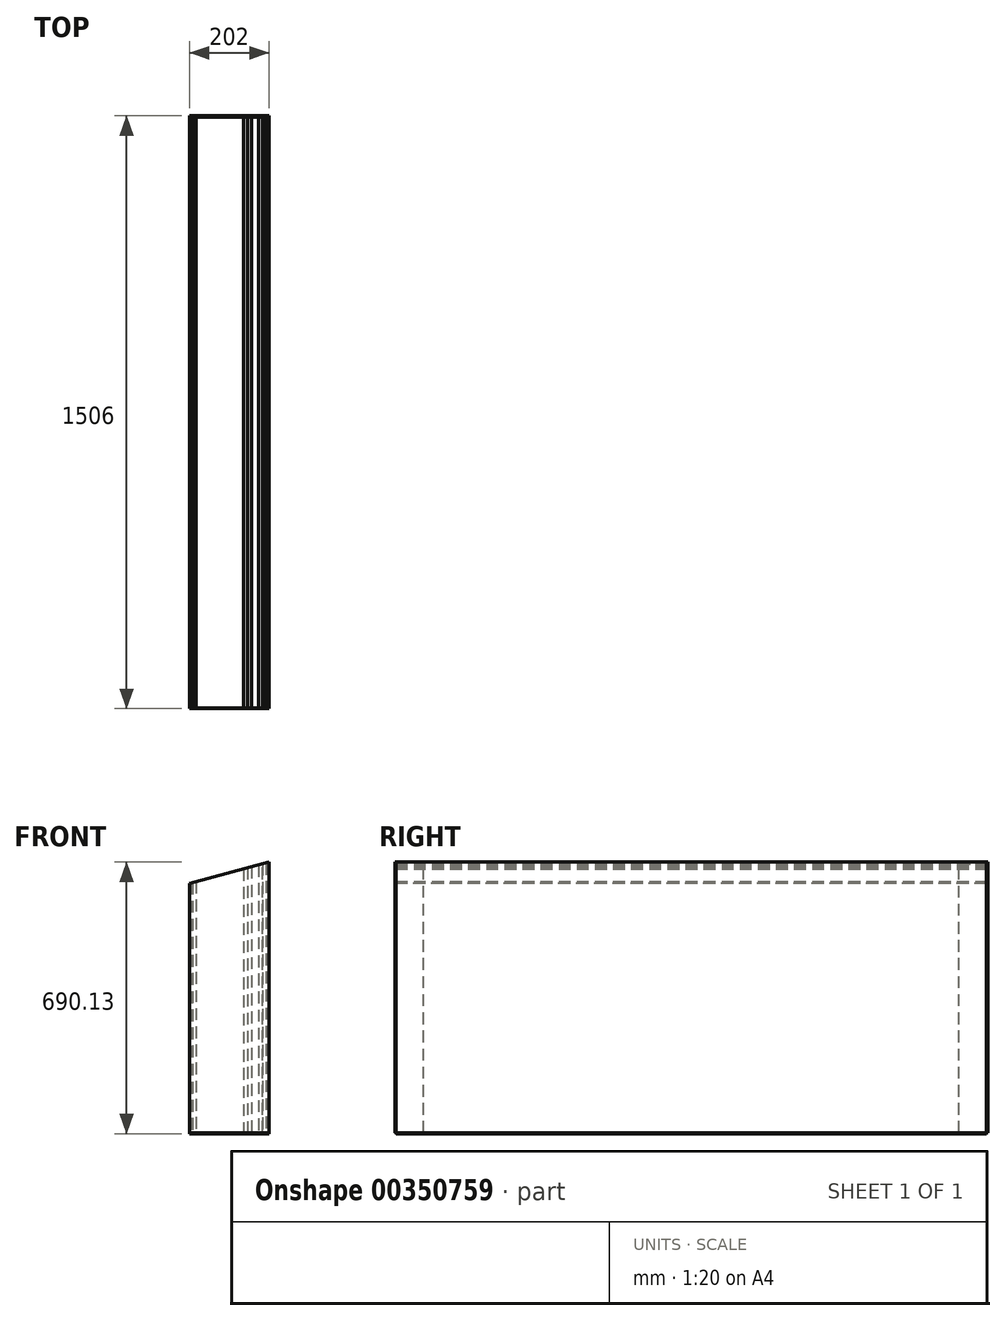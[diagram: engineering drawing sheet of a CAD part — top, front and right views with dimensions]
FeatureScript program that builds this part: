
annotation { "Feature Type Name" : "Feature", "Feature Type Description" : "" }
export const myFeature = defineFeature(function(context is Context, id is Id, definition is map)
    precondition{}
    {
        {
            var Q0;
            Q0=qCreatedBy(makeId("Right.planeOp"),FACE);
            var sketch = newSketch(context, id + "F0", { "sketchPlane" : qUnion([Q0])});
            skLineSegment(sketch, "E0", {"start": v(0, 0) * mm, "end": v(1500, 0) * mm});
            skLineSegment(sketch, "E1", {"start": v(1500, 0) * mm, "end": v(1500, 700) * mm});
            skLineSegment(sketch, "E2", {"start": v(1500, 700) * mm, "end": v(0, 700) * mm});
            skLineSegment(sketch, "E3", {"start": v(0, 700) * mm, "end": v(0, 0) * mm});
            skSolve(sketch);
        }
        {
            var Q0;
            Q0=makeQuery(id+"F0.imprint","IMPRINT",FACE,{"disambiguationData":[TD([[makeQuery(id+"F0.imprint","IMPRINT",EDGE,{"derivedFrom":sQuery(id+"F0.wireOp",EDGE,"E0")}),1.0]])]});
            extrude(context, id + "F1", {"entities" : qUnion([Q0]), "depth" : 6 * mm});
        }
        {
            var Q0;
            Q0=makeQuery(id+"F1.opExtrude","CAP_FACE",FACE,{"disambiguationData":[OSD([sQuery(id+"F0.wireOp",EDGE,"E0"),sQuery(id+"F0.wireOp",EDGE,"E1"),sQuery(id+"F0.wireOp",EDGE,"E2"),sQuery(id+"F0.wireOp",EDGE,"UxQu33BP-PdVc-IvKo-0Oal-Oq9sfbCTzBfW"),sQuery(id+"F0.wireOp",EDGE,"E3")])],"isStart":false});
            extrude(context, id + "F2", {"entities" : qUnion([Q0]), "depth" : 1 * mm});
        }
        {
            var Q0;
            Q0=makeQuery(id+"F2.opExtrude","CAP_FACE",FACE,{"disambiguationData":[OSD([sQuery(id+"F0.wireOp",EDGE,"E0"),sQuery(id+"F0.wireOp",EDGE,"E1"),sQuery(id+"F0.wireOp",EDGE,"E2"),sQuery(id+"F0.wireOp",EDGE,"UxQu33BP-PdVc-IvKo-0Oal-Oq9sfbCTzBfW"),sQuery(id+"F0.wireOp",EDGE,"E3")])],"isStart":false});
            extrude(context, id + "F3", {"entities" : qUnion([Q0]), "depth" : 10 * mm});
        }
        {
            var Q0;
            Q0=makeQuery(id+"F3.opExtrude","CAP_FACE",FACE,{"disambiguationData":[OSD([sQuery(id+"F0.wireOp",EDGE,"E0"),sQuery(id+"F0.wireOp",EDGE,"E1"),sQuery(id+"F0.wireOp",EDGE,"E2"),sQuery(id+"F0.wireOp",EDGE,"UxQu33BP-PdVc-IvKo-0Oal-Oq9sfbCTzBfW"),sQuery(id+"F0.wireOp",EDGE,"E3")])],"isStart":false});
            extrude(context, id + "F4", {"entities" : qUnion([Q0]), "depth" : 120 * mm});
        }
        {
            var Q0;
            Q0=makeQuery(id+"F4.opExtrude","CAP_FACE",FACE,{"disambiguationData":[OSD([sQuery(id+"F0.wireOp",EDGE,"E0"),sQuery(id+"F0.wireOp",EDGE,"E1"),sQuery(id+"F0.wireOp",EDGE,"E2"),sQuery(id+"F0.wireOp",EDGE,"UxQu33BP-PdVc-IvKo-0Oal-Oq9sfbCTzBfW"),sQuery(id+"F0.wireOp",EDGE,"E3")])],"isStart":false});
            extrude(context, id + "F5", {"entities" : qUnion([Q0]), "depth" : 10 * mm});
        }
        {
            var Q0;
            Q0=makeQuery(id+"F5.opExtrude","CAP_FACE",FACE,{"disambiguationData":[OSD([sQuery(id+"F0.wireOp",EDGE,"E0"),sQuery(id+"F0.wireOp",EDGE,"E1"),sQuery(id+"F0.wireOp",EDGE,"E2"),sQuery(id+"F0.wireOp",EDGE,"UxQu33BP-PdVc-IvKo-0Oal-Oq9sfbCTzBfW"),sQuery(id+"F0.wireOp",EDGE,"E3")])],"isStart":false});
            extrude(context, id + "F6", {"entities" : qUnion([Q0]), "depth" : 10 * mm});
        }
        {
            var Q0;
            Q0=makeQuery(id+"F6.opExtrude","CAP_FACE",FACE,{"disambiguationData":[OSD([sQuery(id+"F0.wireOp",EDGE,"E0"),sQuery(id+"F0.wireOp",EDGE,"E1"),sQuery(id+"F0.wireOp",EDGE,"E2"),sQuery(id+"F0.wireOp",EDGE,"UxQu33BP-PdVc-IvKo-0Oal-Oq9sfbCTzBfW"),sQuery(id+"F0.wireOp",EDGE,"E3")])],"isStart":false});
            extrude(context, id + "F7", {"entities" : qUnion([Q0]), "depth" : 18 * mm});
        }
        {
            var Q0;
            Q0=makeQuery(id+"F7.opExtrude","CAP_FACE",FACE,{"disambiguationData":[OSD([sQuery(id+"F0.wireOp",EDGE,"E0"),sQuery(id+"F0.wireOp",EDGE,"E1"),sQuery(id+"F0.wireOp",EDGE,"E2"),sQuery(id+"F0.wireOp",EDGE,"UxQu33BP-PdVc-IvKo-0Oal-Oq9sfbCTzBfW"),sQuery(id+"F0.wireOp",EDGE,"E3")])],"isStart":false});
            extrude(context, id + "F8", {"entities" : qUnion([Q0]), "depth" : 10 * mm});
        }
        {
            var Q0;
            Q0=makeQuery(id+"F8.opExtrude","CAP_FACE",FACE,{"disambiguationData":[OSD([sQuery(id+"F0.wireOp",EDGE,"E0"),sQuery(id+"F0.wireOp",EDGE,"E1"),sQuery(id+"F0.wireOp",EDGE,"E2"),sQuery(id+"F0.wireOp",EDGE,"E3")])],"isStart":false});
            extrude(context, id + "F9", {"entities" : qUnion([Q0]), "depth" : 1 * mm});
        }
        {
            var Q0;
            Q0=makeQuery(id+"F9.opExtrude","CAP_FACE",FACE,{"disambiguationData":[OSD([sQuery(id+"F0.wireOp",EDGE,"E0"),sQuery(id+"F0.wireOp",EDGE,"E1"),sQuery(id+"F0.wireOp",EDGE,"E2"),sQuery(id+"F0.wireOp",EDGE,"E3")])],"isStart":false});
            var sketch = newSketch(context, id + "F10", { "sketchPlane" : qUnion([Q0])});
            skLineSegment(sketch, "E4.bottom", {"start": v(0, 0) * mm, "end": v(70, 0) * mm});
            skLineSegment(sketch, "E4.top", {"start": v(0, 700) * mm, "end": v(70, 700) * mm});
            skLineSegment(sketch, "E4.left", {"start": v(0, 0) * mm, "end": v(0, 700) * mm});
            skLineSegment(sketch, "E4.right", {"start": v(70, 0) * mm, "end": v(70, 700) * mm});
            skLineSegment(sketch, "E5.bottom", {"start": v(1500, 0) * mm, "end": v(1430, 0) * mm});
            skLineSegment(sketch, "E5.top", {"start": v(1500, 700) * mm, "end": v(1430, 700) * mm});
            skLineSegment(sketch, "E5.left", {"start": v(1500, 0) * mm, "end": v(1500, 700) * mm});
            skLineSegment(sketch, "E5.right", {"start": v(1430, 0) * mm, "end": v(1430, 700) * mm});
            skSolve(sketch);
        }
        {
            var Q0;
            Q0=qSketchRegion(id+"F10",true);
            extrude(context, id + "F11", {"entities" : qUnion([Q0]), "depth" : 8 * mm});
        }
        {
            var Q0;
            Q0=makeQuery(id+"F11.opExtrude","CAP_FACE",FACE,{"disambiguationData":[OSD([sQuery(id+"F10.wireOp",EDGE,"E4.bottom"),sQuery(id+"F10.wireOp",EDGE,"E4.top"),sQuery(id+"F10.wireOp",EDGE,"E4.left"),sQuery(id+"F10.wireOp",EDGE,"E4.right")])],"isStart":false});
            var sketch = newSketch(context, id + "F12", { "sketchPlane" : qUnion([Q0])});
            skLineSegment(sketch, "E6.bottom", {"start": v(0, 0) * mm, "end": v(1500, 0) * mm});
            skLineSegment(sketch, "E6.top", {"start": v(0, 700) * mm, "end": v(1500, 700) * mm});
            skLineSegment(sketch, "E6.left", {"start": v(0, 0) * mm, "end": v(0, 700) * mm});
            skLineSegment(sketch, "E6.right", {"start": v(1500, 0) * mm, "end": v(1500, 700) * mm});
            skSolve(sketch);
        }
        {
            var Q0;
            Q0=qSketchRegion(id+"F12",true);
            extrude(context, id + "F13", {"entities" : qUnion([Q0]), "depth" : 8 * mm});
        }
        {
            var Q0;
            Q0=makeQuery(id+"F4.opExtrude","SWEPT_FACE",FACE,{"disambiguationData":[OSD([sQuery(id+"F0.wireOp",EDGE,"E3")])]});
            var sketch = newSketch(context, id + "F14", { "sketchPlane" : qUnion([Q0])});
            skLineSegment(sketch, "E7.bottom", {"start": v(202, 0) * mm, "end": v(0, 0) * mm});
            skLineSegment(sketch, "E7.top", {"start": v(202, 700) * mm, "end": v(0, 700) * mm});
            skLineSegment(sketch, "E7.left", {"start": v(202, 0) * mm, "end": v(202, 700) * mm});
            skLineSegment(sketch, "E7.right", {"start": v(0, 0) * mm, "end": v(0, 700) * mm});
            skSolve(sketch);
        }
        {
            var Q0;
            Q0=qSketchRegion(id+"F14",true);
            extrude(context, id + "F15", {"entities" : qUnion([Q0]), "depth" : 2 * mm});
        }
        {
            var Q0;
            Q0=makeQuery(id+"F4.opExtrude","SWEPT_FACE",FACE,{"disambiguationData":[OSD([sQuery(id+"F0.wireOp",EDGE,"E0")])]});
            var sketch = newSketch(context, id + "F16", { "sketchPlane" : qUnion([Q0])});
            skLineSegment(sketch, "E8.bottom", {"start": v(0, -1500) * mm, "end": v(202, -1500) * mm});
            skLineSegment(sketch, "E8.top", {"start": v(0, 0) * mm, "end": v(202, 0) * mm});
            skLineSegment(sketch, "E8.left", {"start": v(0, -1500) * mm, "end": v(0, 0) * mm});
            skLineSegment(sketch, "E8.right", {"start": v(202, -1500) * mm, "end": v(202, 0) * mm});
            skSolve(sketch);
        }
        {
            var Q0;
            Q0=qSketchRegion(id+"F16",true);
            extrude(context, id + "F17", {"entities" : qUnion([Q0]), "depth" : 2 * mm});
        }
        {
            var Q0;
            Q0=makeQuery(id+"F4.opExtrude","SWEPT_FACE",FACE,{"disambiguationData":[OSD([sQuery(id+"F0.wireOp",EDGE,"E1")])]});
            var sketch = newSketch(context, id + "F18", { "sketchPlane" : qUnion([Q0])});
            skLineSegment(sketch, "E9.bottom", {"start": v(0, 0) * mm, "end": v(-202, 0) * mm});
            skLineSegment(sketch, "E9.top", {"start": v(0, 700) * mm, "end": v(-202, 700) * mm});
            skLineSegment(sketch, "E9.left", {"start": v(0, 0) * mm, "end": v(0, 700) * mm});
            skLineSegment(sketch, "E9.right", {"start": v(-202, 0) * mm, "end": v(-202, 700) * mm});
            skSolve(sketch);
        }
        {
            var Q0;
            Q0=qSketchRegion(id+"F18",true);
            extrude(context, id + "F19", {"entities" : qUnion([Q0]), "depth" : 2 * mm});
        }
        {
            var Q0;
            Q0=makeQuery(id+"F19.opExtrude","CAP_FACE",FACE,{"disambiguationData":[OSD([sQuery(id+"F18.wireOp",EDGE,"E9.bottom"),sQuery(id+"F18.wireOp",EDGE,"E9.top"),sQuery(id+"F18.wireOp",EDGE,"E9.left"),sQuery(id+"F18.wireOp",EDGE,"E9.right")])],"isStart":false});
            extrude(context, id + "F20", {"entities" : qUnion([Q0]), "operationType" : NewBodyOperationType.ADD, "depth" : 2 * mm});
        }
        {
            var Q0;
            Q0=makeQuery(id+"F15.opExtrude","CAP_FACE",FACE,{"disambiguationData":[OSD([sQuery(id+"F14.wireOp",EDGE,"E7.bottom"),sQuery(id+"F14.wireOp",EDGE,"E7.top"),sQuery(id+"F14.wireOp",EDGE,"E7.left"),sQuery(id+"F14.wireOp",EDGE,"E7.right")])],"isStart":false});
            var sketch = newSketch(context, id + "F21", { "sketchPlane" : qUnion([Q0])});
            skLineSegment(sketch, "E10", {"start": v(202, 700) * mm, "end": v(0, 700) * mm});
            skLineSegment(sketch, "E11", {"start": v(0, 700) * mm, "end": v(0, 634) * mm});
            skLineSegment(sketch, "E12", {"start": v(0, 634) * mm, "end": v(202, 688.13) * mm});
            skLineSegment(sketch, "E13", {"start": v(202, 688.13) * mm, "end": v(202, 700) * mm});
            skLineSegment(sketch, "E14", {"start": v(0, 634) * mm, "end": v(0, 0) * mm, "construction": true});
            skSolve(sketch);
        }
        {
            var Q0;
            Q0=makeQuery(id+"F21.imprint","IMPRINT",FACE,{"disambiguationData":[TD([[makeQuery(id+"F21.imprint","IMPRINT",EDGE,{"derivedFrom":sQuery(id+"F21.wireOp",EDGE,"E10")}),1.0]])]});
            extrude(context, id + "F22", {"entities" : qUnion([Q0]), "operationType" : NewBodyOperationType.REMOVE, "endBound" : BoundingType.THROUGH_ALL, "oppositeDirection" : true, "depth" : 25 * mm});
        }
    });
